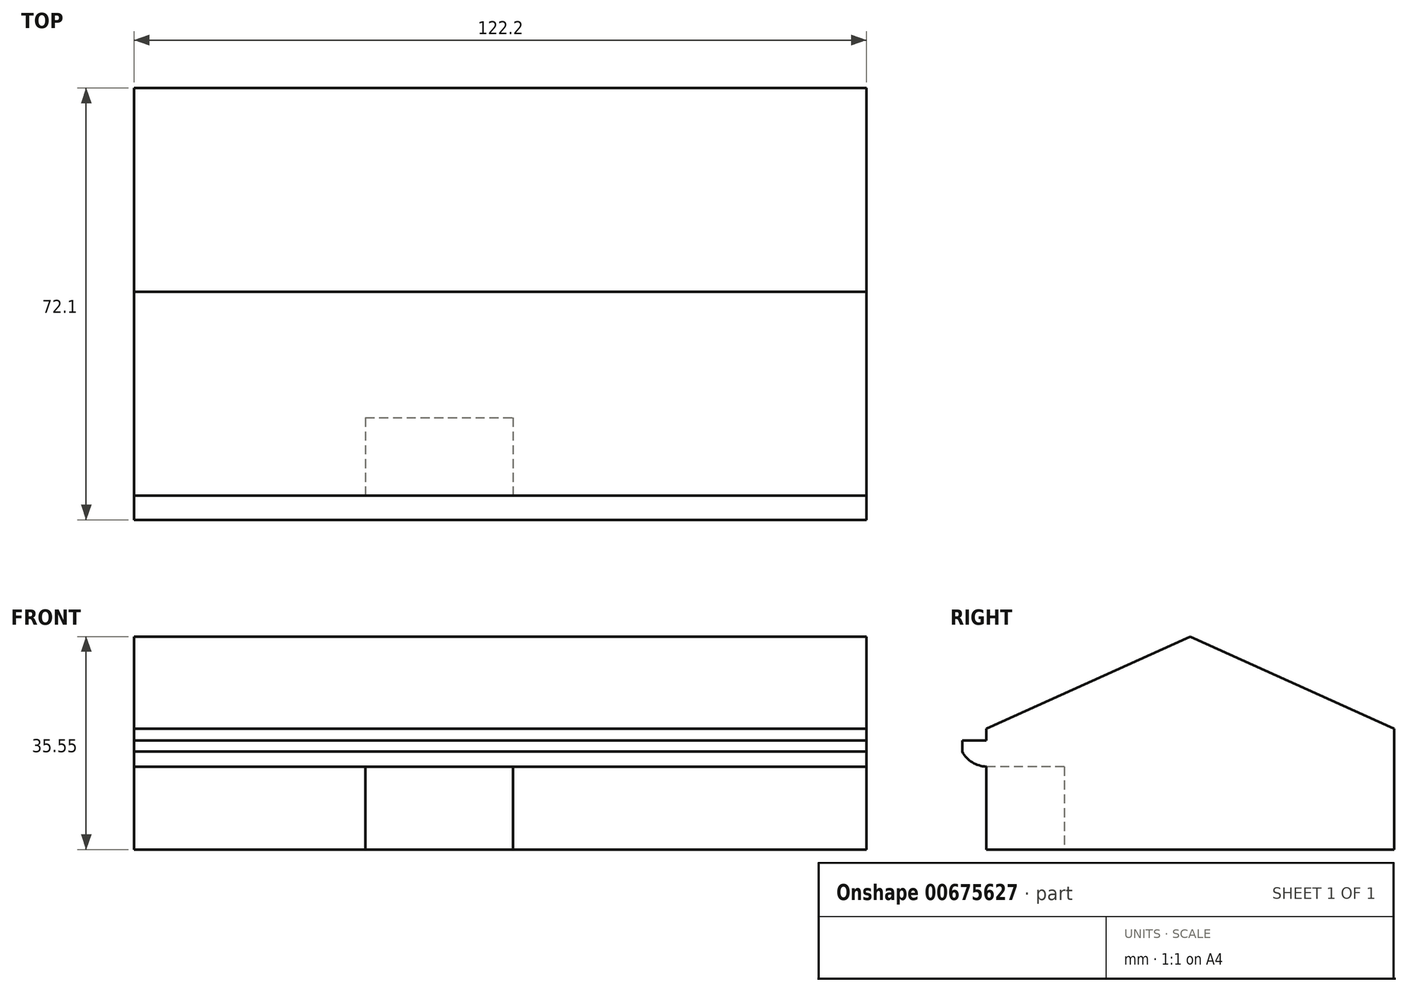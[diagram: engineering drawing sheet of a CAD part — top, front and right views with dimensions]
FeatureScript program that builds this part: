
annotation { "Feature Type Name" : "Feature", "Feature Type Description" : "" }
export const myFeature = defineFeature(function(context is Context, id is Id, definition is map)
    precondition{}
    {
        {
            var Q0;
            Q0=qCreatedBy(makeId("Right.planeOp"),FACE);
            var sketch = newSketch(context, id + "F0", { "sketchPlane" : qUnion([Q0])});
            skLineSegment(sketch, "E0.bottom", {"start": v(0, 0) * mm, "end": v(34.03, 0) * mm});
            skLineSegment(sketch, "E0.top", {"start": v(0, 20.2) * mm, "end": v(34.03, 20.2) * mm});
            skLineSegment(sketch, "E0.left", {"start": v(0, 0) * mm, "end": v(0, 20.2) * mm});
            skLineSegment(sketch, "E0.right", {"start": v(34.03, 0) * mm, "end": v(34.03, 20.2) * mm});
            skLineSegment(sketch, "E1", {"start": v(34.03, 20.2) * mm, "end": v(0, 35.55) * mm});
            skLineSegment(sketch, "E2.MirrorCS", {"start": v(-34.03, 20.2) * mm, "end": v(0, 35.55) * mm});
            skLineSegment(sketch, "E3.MirrorCS", {"start": v(-34.03, 0) * mm, "end": v(-34.03, 20.2) * mm});
            skLineSegment(sketch, "E4.MirrorCS", {"start": v(0, 20.2) * mm, "end": v(-34.03, 20.2) * mm});
            skLineSegment(sketch, "E5.MirrorCS", {"start": v(0, 0) * mm, "end": v(-34.03, 0) * mm});
            skSolve(sketch);
        }
        {
            var Q0;
            Q0 = qSketchRegion(id + "F0", true);
            extrude(context, id + "F1", {"entities" : qUnion([Q0]), "oppositeDirection" : true, "depth" : 50.9 * mm, "offsetDistance" : 25.4 * mm});
        }
        {
            var Q0;
            Q0=makeQuery(id+"F1.opExtrude","CAP_FACE",FACE,{"disambiguationData":[OSD([sQuery(id+"F0.wireOp",EDGE,"E0.bottom"),sQuery(id+"F0.wireOp",EDGE,"E0.right"),sQuery(id+"F0.wireOp",EDGE,"E1"),sQuery(id+"F0.wireOp",EDGE,"E2.MirrorCS"),sQuery(id+"F0.wireOp",EDGE,"E3.MirrorCS"),sQuery(id+"F0.wireOp",EDGE,"E5.MirrorCS")])],"isStart":true});
            extrude(context, id + "F2", {"entities" : qUnion([Q0]), "operationType" : NewBodyOperationType.ADD, "depth" : 71.3 * mm, "offsetDistance" : 25 * mm});
        }
        {
            var Q0;
            {var subQ0=sQuery(id+"F0.wireOp",EDGE,"E3.MirrorCS");Q0=makeQuery(id+"F2.boolean.opBoolean","MERGE",FACE,{"derivedFrom":[makeQuery(id+"F1.opExtrude","SWEPT_FACE",FACE,{"disambiguationData":[OSD([subQ0])]}),makeQuery(id+"F2.opExtrude","SWEPT_FACE",FACE,{"disambiguationData":[OSD([subQ0])]})]});}
            var sketch = newSketch(context, id + "F3", { "sketchPlane" : qUnion([Q0])});
            skLineSegment(sketch, "E6.bottom", {"start": v(-12.3, 13.8) * mm, "end": v(12.3, 13.8) * mm});
            skLineSegment(sketch, "E6.left", {"start": v(-12.3, 13.8) * mm, "end": v(-12.3, 0) * mm});
            skPoint(sketch, "E6.middle", {"position": v(0, -1.96) * mm});
            skLineSegment(sketch, "E7", {"start": v(-12.3, 0) * mm, "end": v(12.3, 0) * mm});
            skPoint(sketch, "E6.top.start.orphan", {"position": v(-12.3, -17.73) * mm});
            skPoint(sketch, "E8.orphan", {"position": v(12.3, -17.73) * mm});
            skLineSegment(sketch, "E9", {"start": v(12.3, 13.8) * mm, "end": v(12.3, 0) * mm});
            skSolve(sketch);
        }
        {
            var Q0;
            Q0=makeQuery(id+"F3.imprint","IMPRINT",FACE,{"disambiguationData":[TD([[makeQuery(id+"F3.imprint","IMPRINT",EDGE,{"derivedFrom":sQuery(id+"F3.wireOp",EDGE,"E6.bottom")}),-1.0]])]});
            extrude(context, id + "F4", {"entities" : qUnion([Q0]), "operationType" : NewBodyOperationType.REMOVE, "oppositeDirection" : true, "depth" : 13 * mm, "offsetDistance" : 25 * mm});
        }
        {
            var Q0;
            Q0=makeQuery(id+"F1.opExtrude","CAP_FACE",FACE,{"disambiguationData":[OSD([sQuery(id+"F0.wireOp",EDGE,"E0.bottom"),sQuery(id+"F0.wireOp",EDGE,"E0.right"),sQuery(id+"F0.wireOp",EDGE,"E1"),sQuery(id+"F0.wireOp",EDGE,"E2.MirrorCS"),sQuery(id+"F0.wireOp",EDGE,"E3.MirrorCS"),sQuery(id+"F0.wireOp",EDGE,"E5.MirrorCS")])],"isStart":false});
            var sketch = newSketch(context, id + "F5", { "sketchPlane" : qUnion([Q0])});
            skLineSegment(sketch, "E10.bottom", {"start": v(34.03, 0) * mm, "end": v(38.07, 0) * mm});
            skLineSegment(sketch, "E10.top", {"start": v(34.03, 18.23) * mm, "end": v(38.07, 18.23) * mm});
            skLineSegment(sketch, "E10.left", {"start": v(34.03, 0) * mm, "end": v(34.03, 18.23) * mm});
            skLineSegment(sketch, "E10.right", {"start": v(38.07, 0) * mm, "end": v(38.07, 18.23) * mm});
            skArc(sketch, "E11", {"start": v(34.03, 13.84) * mm, "mid": v(36.38, 14.55) * mm, "end": v(38.07, 16.33) * mm});
            skSolve(sketch);
        }
        {
            var Q0;
            {var subQ0=sQuery(id+"F5.wireOp",EDGE,"E10.top");Q0=makeQuery(id+"F5.imprint","IMPRINT",FACE,{"disambiguationData":[TD([[makeQuery(id+"F5.imprint","IMPRINT",EDGE,{"derivedFrom":subQ0}),-1.0]])]});}
            extrude(context, id + "F6", {"entities" : qUnion([Q0]), "operationType" : NewBodyOperationType.ADD, "oppositeDirection" : true, "depth" : 122.2 * mm, "offsetDistance" : 25 * mm});
        }
    });
